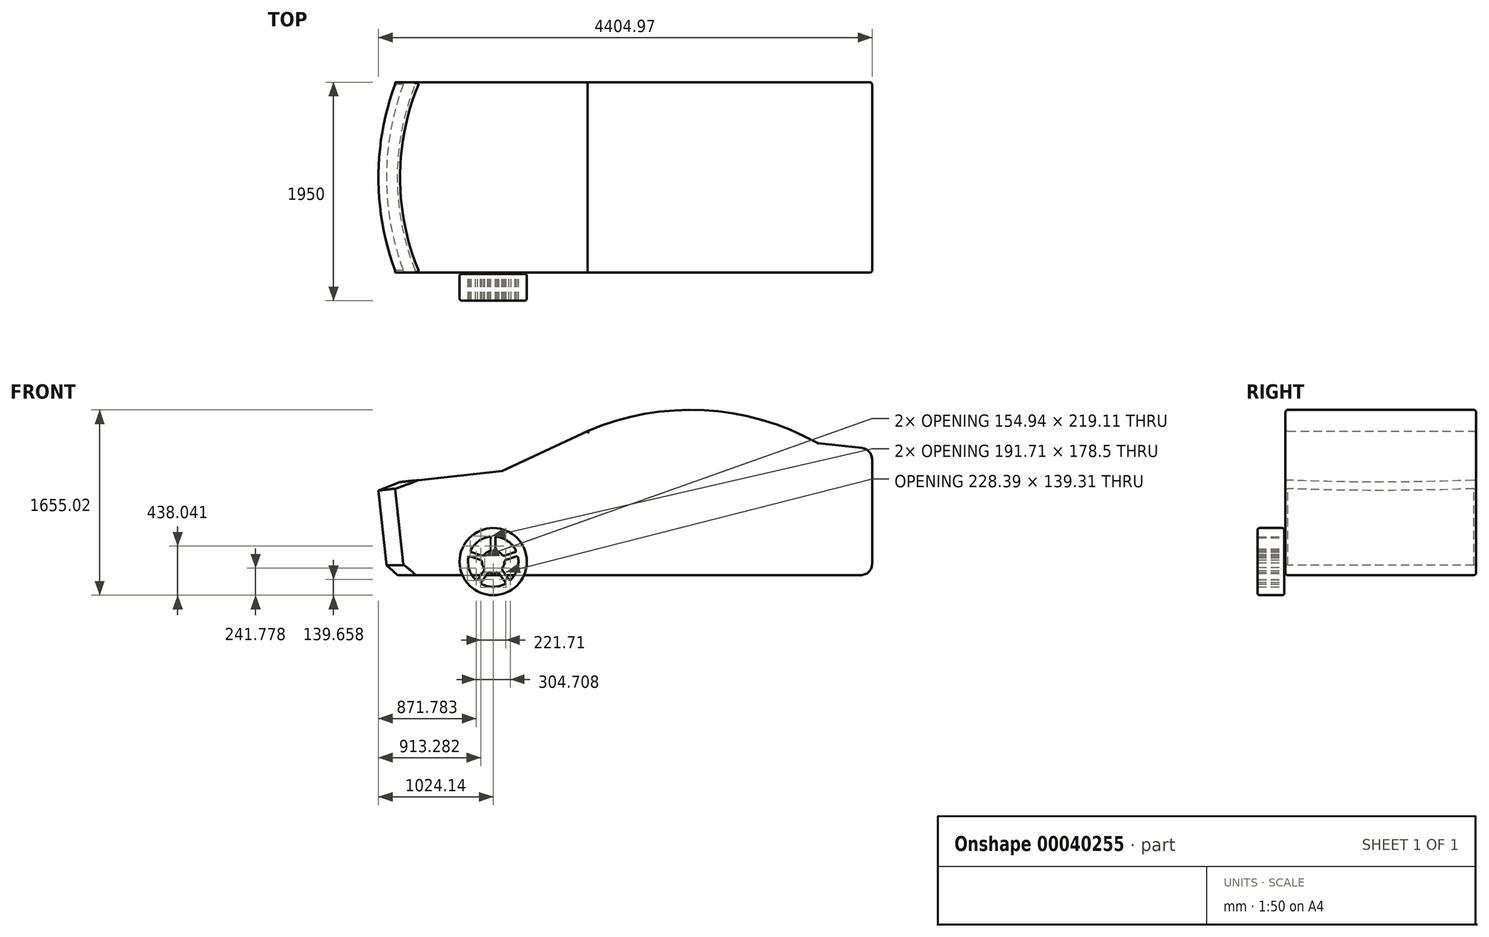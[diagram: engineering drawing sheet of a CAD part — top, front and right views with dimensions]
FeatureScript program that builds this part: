
annotation { "Feature Type Name" : "Feature", "Feature Type Description" : "" }
export const myFeature = defineFeature(function(context is Context, id is Id, definition is map)
    precondition{}
    {
        {
            var Q0;
            Q0=qCreatedBy(makeId("Front.planeOp"),FACE);
            var sketch = newSketch(context, id + "F0", { "sketchPlane" : qUnion([Q0])});
            skLineSegment(sketch, "E0.top", {"start": v(-2132.75, -1125.6) * mm, "end": v(2167.25, -1125.6) * mm});
            skLineSegment(sketch, "E0.left", {"start": v(-2232.75, -415.43) * mm, "end": v(-2232.75, -1025.6) * mm});
            skLineSegment(sketch, "E1", {"start": v(-2232.75, -1125.6) * mm, "end": v(-2232.75, -325.6) * mm, "construction": true});
            skLineSegment(sketch, "E2", {"start": v(-2143.45, -316) * mm, "end": v(-1033.59, -196.63) * mm});
            skLineSegment(sketch, "E3", {"start": v(-1032, -196.19) * mm, "end": v(-272.03, 160.12) * mm});
            skPoint(sketch, "E4.visualSharp", {"position": v(-1032.75, -196.54) * mm});
            skArc(sketch, "E4.filletArc", {"start": v(-1033.59, -196.63) * mm, "mid": v(-1032.77, -196.48) * mm, "end": v(-1032, -196.19) * mm});
            skArc(sketch, "E5", {"start": v(1780.2, 53.7) * mm, "mid": v(766.52, 346.76) * mm, "end": v(-272.03, 160.12) * mm});
            skLineSegment(sketch, "E6", {"start": v(1787.86, 51.26) * mm, "end": v(2177.88, 9.56) * mm});
            skLineSegment(sketch, "E7", {"start": v(2267.25, -89.88) * mm, "end": v(2267.25, -1025.6) * mm});
            skArc(sketch, "E8.filletArc", {"start": v(-2143.45, -316) * mm, "mid": v(-2207.15, -348.6) * mm, "end": v(-2232.75, -415.43) * mm});
            skArc(sketch, "E9.filletArc", {"start": v(-2232.75, -1025.6) * mm, "mid": v(-2203.46, -1096.32) * mm, "end": v(-2132.75, -1125.6) * mm});
            skPoint(sketch, "E10.visualSharp", {"position": v(2267.25, -1125.6) * mm});
            skArc(sketch, "E10.filletArc", {"start": v(2167.25, -1125.6) * mm, "mid": v(2237.96, -1096.32) * mm, "end": v(2267.25, -1025.6) * mm});
            skPoint(sketch, "E11.visualSharp", {"position": v(1783.77, 51.7) * mm});
            skArc(sketch, "E11.filletArc", {"start": v(1780.2, 53.7) * mm, "mid": v(1783.9, 52.1) * mm, "end": v(1787.86, 51.26) * mm});
            skPoint(sketch, "E12.visualSharp", {"position": v(2267.25, 0) * mm});
            skArc(sketch, "E12.filletArc", {"start": v(2267.25, -89.88) * mm, "mid": v(2241.62, -23.03) * mm, "end": v(2177.88, 9.56) * mm});
            skSolve(sketch);
        }
        {
            var Q0;
            Q0=makeQuery(id+"F0.imprint","IMPRINT",FACE,{"disambiguationData":[TD([[makeQuery(id+"F0.imprint","IMPRINT",EDGE,{"derivedFrom":sQuery(id+"F0.wireOp",EDGE,"E0.top")}),1.0]])]});
            extrude(context, id + "F1", {"entities" : qUnion([Q0]), "endBound" : BoundingType.SYMMETRIC, "depth" : 1700 * mm});
        }
        {
            var Q0;
            Q0=makeQuery(id+"F1.opExtrude","CAP_EDGE",EDGE,{"disambiguationData":[OSD([sQuery(id+"F0.wireOp",EDGE,"E0.left")])],"isStart":false});
            var Q1;
            Q1=makeQuery(id+"F1.opExtrude","CAP_EDGE",EDGE,{"disambiguationData":[OSD([sQuery(id+"F0.wireOp",EDGE,"E8.filletArc")])],"isStart":false});
            var Q2;
            Q2=makeQuery(id+"F1.opExtrude","CAP_EDGE",EDGE,{"disambiguationData":[OSD([sQuery(id+"F0.wireOp",EDGE,"E9.filletArc")])],"isStart":false});
            var Q3;
            Q3=makeQuery(id+"F1.opExtrude","CAP_EDGE",EDGE,{"disambiguationData":[OSD([sQuery(id+"F0.wireOp",EDGE,"E8.filletArc")])],"isStart":true});
            var Q4;
            Q4=makeQuery(id+"F1.opExtrude","CAP_EDGE",EDGE,{"disambiguationData":[OSD([sQuery(id+"F0.wireOp",EDGE,"E0.left")])],"isStart":true});
            var Q5;
            Q5=makeQuery(id+"F1.opExtrude","CAP_EDGE",EDGE,{"disambiguationData":[OSD([sQuery(id+"F0.wireOp",EDGE,"E9.filletArc")])],"isStart":true});
            fillet(context, id + "F2", {"entities" : qUnion([Q0, Q1, Q2, Q3, Q4, Q5]), "radius" : 20 * mm, "tangentPropagation" : true, "allowEdgeOverflow" : false});
        }
        {
            var Q0;
            Q0=makeQuery(id+"F1.opExtrude","SWEPT_FACE",FACE,{"disambiguationData":[OSD([sQuery(id+"F0.wireOp",EDGE,"E2")])]});
            var sketch = newSketch(context, id + "F3", { "sketchPlane" : qUnion([Q0])});
            skLineSegment(sketch, "E13", {"start": v(-2164.95, 0) * mm, "end": v(-345.8, 0) * mm, "construction": true});
            skPoint(sketch, "E13.endSnap0", {"position": v(-2164.95, 0) * mm});
            skLineSegment(sketch, "E14", {"start": v(-2164.95, 830) * mm, "end": v(-2014.95, 830) * mm, "construction": true});
            skLineSegment(sketch, "E15", {"start": v(-2014.95, 830) * mm, "end": v(-2014.95, -830) * mm, "construction": true});
            skArc(sketch, "E16", {"start": v(-2014.95, 830) * mm, "mid": v(-2164.95, 0) * mm, "end": v(-2014.95, -830) * mm});
            skLineSegment(sketch, "E17", {"start": v(-2014.95, 830) * mm, "end": v(-2014.95, 1337.98) * mm});
            skLineSegment(sketch, "E18", {"start": v(-2014.95, 1337.98) * mm, "end": v(-2457.8, 1337.98) * mm});
            skLineSegment(sketch, "E19", {"start": v(-2457.8, -1053.15) * mm, "end": v(-2457.8, 1337.98) * mm});
            skLineSegment(sketch, "E20", {"start": v(-2457.8, -1053.15) * mm, "end": v(-2015.56, -1053.15) * mm});
            skLineSegment(sketch, "E21", {"start": v(-2014.95, -830) * mm, "end": v(-2015.56, -1053.15) * mm});
            skSolve(sketch);
        }
        {
            var Q0;
            {var subQ8=sQuery(id+"F3.wireOp",EDGE,"E17");Q0=makeQuery(id+"F3.imprint","IMPRINT",FACE,{"disambiguationData":[TD([[makeQuery(id+"F3.imprint","IMPRINT",EDGE,{"derivedFrom":subQ8}),1.0]])]});}
            var Q1;
            {var subQ0=sQuery(id+"F0.wireOp",EDGE,"E2");var subQ2=sQuery(id+"F3.wireOp",EDGE,"E16");var subQ4=makeQuery(id+"F1.opExtrude","SWEPT_EDGE",EDGE,{"disambiguationData":[OSD([subQ0,sQuery(id+"F0.wireOp",EDGE,"E8.filletArc")])]});var subQ6=makeQuery(id+"F3.imprint","INTERSECT",VERTEX,{"derivedFrom":[subQ4,subQ2]});Q1=makeQuery(id+"F3.imprint","IMPRINT",FACE,{"disambiguationData":[TD([[makeQuery(id+"F3.imprint","IMPRINT",EDGE,{"disambiguationData":[TD([[subQ6,1.0]])],"derivedFrom":subQ2}),-1.0]])]});}
            var Q2;
            {var subQ0=sQuery(id+"F0.wireOp",EDGE,"E2");var subQ2=sQuery(id+"F3.wireOp",EDGE,"E16");var subQ4=makeQuery(id+"F1.opExtrude","SWEPT_EDGE",EDGE,{"disambiguationData":[OSD([subQ0,sQuery(id+"F0.wireOp",EDGE,"E8.filletArc")])]});var subQ6=makeQuery(id+"F3.imprint","INTERSECT",VERTEX,{"derivedFrom":[subQ4,subQ2]});Q2=makeQuery(id+"F3.imprint","IMPRINT",FACE,{"disambiguationData":[TD([[makeQuery(id+"F3.imprint","IMPRINT",EDGE,{"disambiguationData":[TD([[subQ6,-1.0]])],"derivedFrom":subQ2}),-1.0]])]});}
            var Q3;
            Q3=sQuery(id+"F3.wireOp",EDGE,"E18");
            var Q4;
            Q4=sQuery(id+"F3.wireOp",EDGE,"E16");
            var Q5;
            Q5=sQuery(id+"F3.wireOp",EDGE,"E17");
            var Q6;
            Q6=sQuery(id+"F3.wireOp",EDGE,"E19");
            var Q7;
            Q7=sQuery(id+"F3.wireOp",EDGE,"E20");
            var Q8;
            Q8=sQuery(id+"F3.wireOp",EDGE,"E21");
            extrude(context, id + "F4", {"entities" : qUnion([Q0, Q1, Q2]), "operationType" : NewBodyOperationType.REMOVE, "surfaceEntities" : qUnion([Q3, Q4, Q5, Q6, Q7, Q8]), "endBound" : BoundingType.SYMMETRIC, "oppositeDirection" : true, "depth" : 2000 * mm});
        }
        {
            var Q0;
            Q0=makeQuery(id+"F4.boolean.opBoolean","INTERSECT",EDGE,{"derivedFrom":[makeQuery(id+"F1.opExtrude","SWEPT_FACE",FACE,{"disambiguationData":[OSD([sQuery(id+"F0.wireOp",EDGE,"E0.top")])]}),makeQuery(id+"F4.opExtrude","SWEPT_FACE",FACE,{"disambiguationData":[OSD([sQuery(id+"F3.wireOp",EDGE,"E16")])]})]});
            chamfer(context, id + "F5", {"entities" : qUnion([Q0]), "width" : 100 * mm, "tangentPropagation" : true});
        }
        {
            var Q0;
            Q0=makeQuery(id+"F4.boolean.opBoolean","INTERSECT",EDGE,{"derivedFrom":[makeQuery(id+"F1.opExtrude","SWEPT_FACE",FACE,{"disambiguationData":[OSD([sQuery(id+"F0.wireOp",EDGE,"E2")])]}),makeQuery(id+"F4.opExtrude","SWEPT_FACE",FACE,{"disambiguationData":[OSD([sQuery(id+"F3.wireOp",EDGE,"E16")])]})]});
            chamfer(context, id + "F6", {"entities" : qUnion([Q0]), "chamferType" : ChamferType.OFFSET_ANGLE, "width" : 200 * mm, "oppositeDirection" : false, "angle" : 15 * degree, "tangentPropagation" : true});
        }
        {
            var Q0;
            Q0=makeQuery(id+"F1.opExtrude","CAP_FACE",FACE,{"disambiguationData":[OSD([sQuery(id+"F0.wireOp",EDGE,"E0.top"),sQuery(id+"F0.wireOp",EDGE,"E0.left"),sQuery(id+"F0.wireOp",EDGE,"E2"),sQuery(id+"F0.wireOp",EDGE,"E3"),sQuery(id+"F0.wireOp",EDGE,"E4.filletArc"),sQuery(id+"F0.wireOp",EDGE,"E5"),sQuery(id+"F0.wireOp",EDGE,"E6"),sQuery(id+"F0.wireOp",EDGE,"E7"),sQuery(id+"F0.wireOp",EDGE,"E8.filletArc"),sQuery(id+"F0.wireOp",EDGE,"E9.filletArc"),sQuery(id+"F0.wireOp",EDGE,"E10.filletArc"),sQuery(id+"F0.wireOp",EDGE,"E11.filletArc"),sQuery(id+"F0.wireOp",EDGE,"E12.filletArc")])],"isStart":false});
            var sketch = newSketch(context, id + "F7", { "sketchPlane" : qUnion([Q0])});
            skLineSegment(sketch, "E22", {"start": v(-2113.58, -355.15) * mm, "end": v(-1113.58, -355.15) * mm, "construction": true});
            skLineSegment(sketch, "E23", {"start": v(-1113.58, -355.15) * mm, "end": v(-1113.58, -780.15) * mm, "construction": true});
            skCircle(sketch, "E24", {"center": v(-1113.58, -1005.15) * mm, "radius": 300 * mm});
            skLineSegment(sketch, "E25", {"start": v(-1113.58, -355.15) * mm, "end": v(2247.25, -355.15) * mm, "construction": true});
            skLineSegment(sketch, "E26", {"start": v(1247.25, -355.15) * mm, "end": v(1247.25, -1269.77) * mm, "construction": true});
            skCircle(sketch, "E27", {"center": v(1247.25, -1005.15) * mm, "radius": 300 * mm});
            skCircle(sketch, "E28", {"center": v(-1113.58, -1005.15) * mm, "radius": 100 * mm});
            skArc(sketch, "E29.0", {"start": v(-1023.5, -214.3) * mm, "mid": v(-1027.38, -215.74) * mm, "end": v(-1031.45, -216.52) * mm});
            skLineSegment(sketch, "E29.1", {"start": v(-263.82, 141.88) * mm, "end": v(-1023.5, -214.3) * mm});
            skLineSegment(sketch, "E29.2", {"start": v(-1814.07, -1105.6) * mm, "end": v(2167.25, -1105.6) * mm});
            skFitSpline(sketch, "E29.3", {"points": [v(-1917.03, -1018.95) * mm, v(-1882.07, -1048.45) * mm, v(-1847.75, -1077.34) * mm, v(-1814.07, -1105.6) * mm]});
            skLineSegment(sketch, "E29.4", {"start": v(-1988.43, -355.15) * mm, "end": v(-1917.03, -1018.95) * mm});
            skFitSpline(sketch, "E29.5", {"points": [v(-1850.57, -304.62) * mm, v(-1896.54, -321.41) * mm, v(-1942.5, -338.26) * mm, v(-1988.43, -355.15) * mm]});
            skArc(sketch, "E29.6", {"start": v(2167.25, -1105.6) * mm, "mid": v(2223.81, -1082.18) * mm, "end": v(2247.25, -1025.6) * mm});
            skLineSegment(sketch, "E29.7", {"start": v(2247.25, -1025.6) * mm, "end": v(2247.25, -89.88) * mm});
            skLineSegment(sketch, "E29.8", {"start": v(-1031.45, -216.52) * mm, "end": v(-1850.57, -304.62) * mm});
            skArc(sketch, "E29.9", {"start": v(2247.25, -89.88) * mm, "mid": v(2226.75, -36.4) * mm, "end": v(2175.75, -10.33) * mm});
            skLineSegment(sketch, "E29.10", {"start": v(2175.75, -10.33) * mm, "end": v(1785.74, 31.37) * mm});
            skArc(sketch, "E29.11", {"start": v(1785.74, 31.37) * mm, "mid": v(1777.83, 33.04) * mm, "end": v(1770.42, 36.26) * mm});
            skArc(sketch, "E29.12", {"start": v(1770.42, 36.26) * mm, "mid": v(765.64, 326.78) * mm, "end": v(-263.82, 141.88) * mm});
            skLineSegment(sketch, "E30", {"start": v(-1133.58, -781.04) * mm, "end": v(-1148.86, -782.93) * mm, "construction": true});
            skArc(sketch, "E31", {"start": v(-1133.58, -793.8) * mm, "mid": v(-1139.1, -785.4) * mm, "end": v(-1148.86, -782.93) * mm});
            skArc(sketch, "E32.MirrorCS", {"start": v(-1093.58, -793.8) * mm, "mid": v(-1088.06, -785.4) * mm, "end": v(-1078.3, -782.93) * mm});
            skLineSegment(sketch, "E33", {"start": v(-1113.58, -780.15) * mm, "end": v(-1113.58, -905.15) * mm, "construction": true});
            skLineSegment(sketch, "E34", {"start": v(-1113.58, -905.15) * mm, "end": v(-1113.58, -1251.07) * mm, "construction": true});
            skLineSegment(sketch, "E35", {"start": v(-1113.58, -842.65) * mm, "end": v(-1183.72, -842.65) * mm, "construction": true});
            skLineSegment(sketch, "E36", {"start": v(-1183.72, -842.65) * mm, "end": v(-1054.84, -842.65) * mm, "construction": true});
            skArc(sketch, "E37", {"start": v(-1093.58, -891.02) * mm, "mid": v(-1087.72, -904.83) * mm, "end": v(-1075.05, -912.87) * mm});
            skArc(sketch, "E38.MirrorCS", {"start": v(-1133.58, -891.02) * mm, "mid": v(-1139.45, -904.83) * mm, "end": v(-1152.11, -912.87) * mm});
            skLineSegment(sketch, "E39", {"start": v(-1133.58, -891.02) * mm, "end": v(-1133.58, -793.8) * mm});
            skLineSegment(sketch, "E40", {"start": v(-1093.58, -891.02) * mm, "end": v(-1093.58, -793.8) * mm});
            skArc(sketch, "E41.1.0", {"start": v(1254.24, -584.81) * mm, "mid": v(1249.73, -593.8) * mm, "end": v(1252.47, -603.48) * mm});
            skLineSegment(sketch, "E41.1.1", {"start": v(1338.44, -536.2) * mm, "end": v(1254.24, -584.81) * mm});
            skArc(sketch, "E41.1.2", {"start": v(1338.44, -536.2) * mm, "mid": v(1353.33, -534.38) * mm, "end": v(1366.62, -541.32) * mm});
            skArc(sketch, "E41.1.3", {"start": v(1318.44, -501.56) * mm, "mid": v(1327.46, -489.58) * mm, "end": v(1328.1, -474.59) * mm});
            skLineSegment(sketch, "E41.1.4", {"start": v(1318.44, -501.56) * mm, "end": v(1234.24, -550.17) * mm});
            skArc(sketch, "E41.1.5", {"start": v(1234.24, -550.17) * mm, "mid": v(1224.2, -549.59) * mm, "end": v(1217.2, -542.38) * mm});
            skArc(sketch, "E41.2.0", {"start": v(-120.66, 1378.61) * mm, "mid": v(-110.62, 1379.2) * mm, "end": v(-103.6, 1386.4) * mm});
            skLineSegment(sketch, "E41.2.1", {"start": v(-204.85, 1427.22) * mm, "end": v(-120.66, 1378.61) * mm});
            skArc(sketch, "E41.2.2", {"start": v(-204.85, 1427.22) * mm, "mid": v(-213.88, 1439.2) * mm, "end": v(-214.51, 1454.2) * mm});
            skArc(sketch, "E41.2.3", {"start": v(-224.85, 1392.58) * mm, "mid": v(-239.74, 1394.4) * mm, "end": v(-253.04, 1387.46) * mm});
            skLineSegment(sketch, "E41.2.4", {"start": v(-224.85, 1392.58) * mm, "end": v(-140.66, 1343.97) * mm});
            skArc(sketch, "E41.2.5", {"start": v(-140.66, 1343.97) * mm, "mid": v(-136.14, 1334.98) * mm, "end": v(-138.88, 1325.3) * mm});
            skPoint(sketch, "E41.center", {"position": v(0, 0) * mm});
            skLineSegment(sketch, "E42.1.0", {"start": v(-1215.94, -950.86) * mm, "end": v(-1308.4, -920.82) * mm});
            skArc(sketch, "E42.1.1", {"start": v(-1215.94, -950.86) * mm, "mid": v(-1201, -949.55) * mm, "end": v(-1189.44, -939.99) * mm});
            skArc(sketch, "E42.1.2", {"start": v(-1228.3, -988.9) * mm, "mid": v(-1216.99, -998.75) * mm, "end": v(-1213.25, -1013.28) * mm});
            skLineSegment(sketch, "E42.1.3", {"start": v(-1228.3, -988.9) * mm, "end": v(-1320.77, -958.86) * mm});
            skArc(sketch, "E42.1.4", {"start": v(-1308.4, -920.82) * mm, "mid": v(-1314.7, -912.96) * mm, "end": v(-1314.02, -902.93) * mm});
            skArc(sketch, "E42.1.5", {"start": v(-1320.77, -958.86) * mm, "mid": v(-1330.47, -961.52) * mm, "end": v(-1335.83, -970.03) * mm});
            skLineSegment(sketch, "E42.2.0", {"start": v(-1196.85, -1085.72) * mm, "end": v(-1254, -1164.38) * mm});
            skArc(sketch, "E42.2.1", {"start": v(-1196.85, -1085.72) * mm, "mid": v(-1193.48, -1071.1) * mm, "end": v(-1199, -1057.16) * mm});
            skArc(sketch, "E42.2.2", {"start": v(-1164.49, -1109.24) * mm, "mid": v(-1151.62, -1101.51) * mm, "end": v(-1136.65, -1102.45) * mm});
            skLineSegment(sketch, "E42.2.3", {"start": v(-1164.49, -1109.24) * mm, "end": v(-1221.63, -1187.9) * mm});
            skArc(sketch, "E42.2.4", {"start": v(-1254, -1164.38) * mm, "mid": v(-1263.4, -1167.93) * mm, "end": v(-1272.74, -1164.2) * mm});
            skArc(sketch, "E42.2.5", {"start": v(-1221.63, -1187.9) * mm, "mid": v(-1222.1, -1197.94) * mm, "end": v(-1215.66, -1205.66) * mm});
            skLineSegment(sketch, "E42.3.0", {"start": v(-1062.68, -1109.24) * mm, "end": v(-1005.53, -1187.9) * mm});
            skArc(sketch, "E42.3.1", {"start": v(-1062.68, -1109.24) * mm, "mid": v(-1075.54, -1101.51) * mm, "end": v(-1090.51, -1102.45) * mm});
            skArc(sketch, "E42.3.2", {"start": v(-1030.32, -1085.72) * mm, "mid": v(-1033.7, -1071.1) * mm, "end": v(-1028.17, -1057.16) * mm});
            skLineSegment(sketch, "E42.3.3", {"start": v(-1030.32, -1085.72) * mm, "end": v(-973.17, -1164.38) * mm});
            skArc(sketch, "E42.3.4", {"start": v(-1005.53, -1187.9) * mm, "mid": v(-1005.07, -1197.94) * mm, "end": v(-1011.5, -1205.66) * mm});
            skArc(sketch, "E42.3.5", {"start": v(-973.17, -1164.38) * mm, "mid": v(-963.76, -1167.93) * mm, "end": v(-954.43, -1164.2) * mm});
            skLineSegment(sketch, "E42.4.0", {"start": v(-998.86, -988.9) * mm, "end": v(-906.4, -958.86) * mm});
            skArc(sketch, "E42.4.1", {"start": v(-998.86, -988.9) * mm, "mid": v(-1010.18, -998.75) * mm, "end": v(-1013.91, -1013.28) * mm});
            skArc(sketch, "E42.4.2", {"start": v(-1011.22, -950.86) * mm, "mid": v(-1026.17, -949.55) * mm, "end": v(-1037.73, -939.99) * mm});
            skLineSegment(sketch, "E42.4.3", {"start": v(-1011.22, -950.86) * mm, "end": v(-918.76, -920.82) * mm});
            skArc(sketch, "E42.4.4", {"start": v(-906.4, -958.86) * mm, "mid": v(-896.7, -961.52) * mm, "end": v(-891.34, -970.03) * mm});
            skArc(sketch, "E42.4.5", {"start": v(-918.76, -920.82) * mm, "mid": v(-912.47, -912.96) * mm, "end": v(-913.14, -902.93) * mm});
            skArc(sketch, "E43", {"start": v(-1148.86, -782.93) * mm, "mid": v(-1245.83, -823.12) * mm, "end": v(-1314.02, -902.93) * mm});
            skArc(sketch, "E44", {"start": v(-1335.83, -970.03) * mm, "mid": v(-1327.57, -1074.68) * mm, "end": v(-1272.74, -1164.2) * mm});
            skArc(sketch, "E45", {"start": v(-1215.66, -1205.66) * mm, "mid": v(-1113.58, -1230.15) * mm, "end": v(-1011.5, -1205.66) * mm});
            skArc(sketch, "E46", {"start": v(-954.43, -1164.2) * mm, "mid": v(-899.6, -1074.68) * mm, "end": v(-891.34, -970.03) * mm});
            skArc(sketch, "E47", {"start": v(-913.14, -902.93) * mm, "mid": v(-981.33, -823.12) * mm, "end": v(-1078.3, -782.93) * mm});
            skSolve(sketch);
        }
        {
            var Q0;
            Q0=makeQuery(id+"F7.imprint","IMPRINT",FACE,{"disambiguationData":[TD([[makeQuery(id+"F7.imprint","IMPRINT",EDGE,{"derivedFrom":sQuery(id+"F7.wireOp",EDGE,"E31")}),-1.0]])]});
            var Q1;
            {var subQ15=sQuery(id+"F7.wireOp",EDGE,"E42.2.3");Q1=makeQuery(id+"F7.imprint","IMPRINT",FACE,{"disambiguationData":[TD([[makeQuery(id+"F7.imprint","IMPRINT",EDGE,{"derivedFrom":subQ15}),-1.0]])]});}
            var Q2;
            {var subQ3=sQuery(id+"F7.wireOp",EDGE,"E28");var subQ5=sQuery(id+"F7.wireOp",EDGE,"E42.2.1");var subQ6=makeQuery(id+"F7.imprint","INTERSECT",VERTEX,{"disambiguationData":[OD(1.0)],"derivedFrom":[subQ3,subQ5]});Q2=makeQuery(id+"F7.imprint","IMPRINT",FACE,{"disambiguationData":[TD([[makeQuery(id+"F7.imprint","IMPRINT",EDGE,{"disambiguationData":[TD([[subQ6,-1.0]])],"derivedFrom":subQ3}),-1.0]])]});}
            var Q3;
            {var subQ5=sQuery(id+"F7.wireOp",EDGE,"E28");var subQ7=sQuery(id+"F7.wireOp",EDGE,"E42.3.1");var subQ8=makeQuery(id+"F7.imprint","INTERSECT",VERTEX,{"disambiguationData":[OD(1.0)],"derivedFrom":[subQ5,subQ7]});Q3=makeQuery(id+"F7.imprint","IMPRINT",FACE,{"disambiguationData":[TD([[makeQuery(id+"F7.imprint","IMPRINT",EDGE,{"disambiguationData":[TD([[subQ8,-1.0]])],"derivedFrom":subQ5}),-1.0]])]});}
            var Q4;
            {var subQ1=sQuery(id+"F7.wireOp",EDGE,"E28");var subQ16=sQuery(id+"F7.wireOp",EDGE,"E37");var subQ18=makeQuery(id+"F7.imprint","INTERSECT",VERTEX,{"disambiguationData":[OD(0.0)],"derivedFrom":[subQ1,subQ16]});Q4=makeQuery(id+"F7.imprint","IMPRINT",FACE,{"disambiguationData":[TD([[makeQuery(id+"F7.imprint","IMPRINT",EDGE,{"disambiguationData":[TD([[subQ18,1.0]])],"derivedFrom":subQ1}),1.0]])]});}
            extrude(context, id + "F8", {"entities" : qUnion([Q0, Q1, Q2, Q3, Q4]), "operationType" : NewBodyOperationType.ADD, "depth" : 250 * mm, "hasSecondDirection" : true, "secondDirectionOppositeDirection" : false, "secondDirectionDepth" : 10 * mm});
        }
        {
            var Q0;
            Q0=makeQuery(id+"F8.opExtrude","CAP_EDGE",EDGE,{"disambiguationData":[OSD([sQuery(id+"F7.wireOp",EDGE,"E24")])],"isStart":false});
            fillet(context, id + "F9", {"entities" : qUnion([Q0]), "radius" : 20 * mm, "tangentPropagation" : true, "allowEdgeOverflow" : false});
        }
        {
            var Q0;
            Q0=makeQuery(id+"F8.opExtrude","CAP_FACE",FACE,{"disambiguationData":[OSD([sQuery(id+"F7.wireOp",EDGE,"E24"),sQuery(id+"F7.wireOp",EDGE,"E28"),sQuery(id+"F7.wireOp",EDGE,"E31"),sQuery(id+"F7.wireOp",EDGE,"E32.MirrorCS"),sQuery(id+"F7.wireOp",EDGE,"E37"),sQuery(id+"F7.wireOp",EDGE,"E38.MirrorCS"),sQuery(id+"F7.wireOp",EDGE,"E39"),sQuery(id+"F7.wireOp",EDGE,"E40"),sQuery(id+"F7.wireOp",EDGE,"E42.1.0"),sQuery(id+"F7.wireOp",EDGE,"E42.1.1"),sQuery(id+"F7.wireOp",EDGE,"E42.1.2"),sQuery(id+"F7.wireOp",EDGE,"E42.1.3"),sQuery(id+"F7.wireOp",EDGE,"E42.1.4"),sQuery(id+"F7.wireOp",EDGE,"E42.1.5"),sQuery(id+"F7.wireOp",EDGE,"E42.2.0"),sQuery(id+"F7.wireOp",EDGE,"E42.2.1"),sQuery(id+"F7.wireOp",EDGE,"E42.2.2"),sQuery(id+"F7.wireOp",EDGE,"E42.2.3"),sQuery(id+"F7.wireOp",EDGE,"E42.2.4"),sQuery(id+"F7.wireOp",EDGE,"E42.2.5"),sQuery(id+"F7.wireOp",EDGE,"E42.3.0"),sQuery(id+"F7.wireOp",EDGE,"E42.3.1"),sQuery(id+"F7.wireOp",EDGE,"E42.3.2"),sQuery(id+"F7.wireOp",EDGE,"E42.3.3"),sQuery(id+"F7.wireOp",EDGE,"E42.3.4"),sQuery(id+"F7.wireOp",EDGE,"E42.3.5"),sQuery(id+"F7.wireOp",EDGE,"E42.4.0"),sQuery(id+"F7.wireOp",EDGE,"E42.4.1"),sQuery(id+"F7.wireOp",EDGE,"E42.4.2"),sQuery(id+"F7.wireOp",EDGE,"E42.4.3"),sQuery(id+"F7.wireOp",EDGE,"E42.4.4"),sQuery(id+"F7.wireOp",EDGE,"E42.4.5"),sQuery(id+"F7.wireOp",EDGE,"E43"),sQuery(id+"F7.wireOp",EDGE,"E44"),sQuery(id+"F7.wireOp",EDGE,"E45"),sQuery(id+"F7.wireOp",EDGE,"E46"),sQuery(id+"F7.wireOp",EDGE,"E47")])],"isStart":false});
            fillet(context, id + "F10", {"entities" : qUnion([Q0]), "radius" : 5 * mm, "tangentPropagation" : true, "allowEdgeOverflow" : false});
        }
        {
            var Q0;
            Q0=makeQuery(id+"F8.opExtrude","CAP_EDGE",EDGE,{"disambiguationData":[OSD([sQuery(id+"F7.wireOp",EDGE,"E24")])],"isStart":true});
            fillet(context, id + "F11", {"entities" : qUnion([Q0]), "radius" : 20 * mm, "tangentPropagation" : true, "allowEdgeOverflow" : false});
        }
        {
            var Q0;
            Q0=makeQuery(id+"F8.opExtrude","CAP_FACE",FACE,{"disambiguationData":[OSD([sQuery(id+"F7.wireOp",EDGE,"E24"),sQuery(id+"F7.wireOp",EDGE,"E28"),sQuery(id+"F7.wireOp",EDGE,"E31"),sQuery(id+"F7.wireOp",EDGE,"E32.MirrorCS"),sQuery(id+"F7.wireOp",EDGE,"E37"),sQuery(id+"F7.wireOp",EDGE,"E38.MirrorCS"),sQuery(id+"F7.wireOp",EDGE,"E39"),sQuery(id+"F7.wireOp",EDGE,"E40"),sQuery(id+"F7.wireOp",EDGE,"E42.1.0"),sQuery(id+"F7.wireOp",EDGE,"E42.1.1"),sQuery(id+"F7.wireOp",EDGE,"E42.1.2"),sQuery(id+"F7.wireOp",EDGE,"E42.1.3"),sQuery(id+"F7.wireOp",EDGE,"E42.1.4"),sQuery(id+"F7.wireOp",EDGE,"E42.1.5"),sQuery(id+"F7.wireOp",EDGE,"E42.2.0"),sQuery(id+"F7.wireOp",EDGE,"E42.2.1"),sQuery(id+"F7.wireOp",EDGE,"E42.2.2"),sQuery(id+"F7.wireOp",EDGE,"E42.2.3"),sQuery(id+"F7.wireOp",EDGE,"E42.2.4"),sQuery(id+"F7.wireOp",EDGE,"E42.2.5"),sQuery(id+"F7.wireOp",EDGE,"E42.3.0"),sQuery(id+"F7.wireOp",EDGE,"E42.3.1"),sQuery(id+"F7.wireOp",EDGE,"E42.3.2"),sQuery(id+"F7.wireOp",EDGE,"E42.3.3"),sQuery(id+"F7.wireOp",EDGE,"E42.3.4"),sQuery(id+"F7.wireOp",EDGE,"E42.3.5"),sQuery(id+"F7.wireOp",EDGE,"E42.4.0"),sQuery(id+"F7.wireOp",EDGE,"E42.4.1"),sQuery(id+"F7.wireOp",EDGE,"E42.4.2"),sQuery(id+"F7.wireOp",EDGE,"E42.4.3"),sQuery(id+"F7.wireOp",EDGE,"E42.4.4"),sQuery(id+"F7.wireOp",EDGE,"E42.4.5"),sQuery(id+"F7.wireOp",EDGE,"E43"),sQuery(id+"F7.wireOp",EDGE,"E44"),sQuery(id+"F7.wireOp",EDGE,"E45"),sQuery(id+"F7.wireOp",EDGE,"E46"),sQuery(id+"F7.wireOp",EDGE,"E47")])],"isStart":true});
            fillet(context, id + "F12", {"entities" : qUnion([Q0]), "radius" : 5 * mm, "tangentPropagation" : true, "allowEdgeOverflow" : false});
        }
    });
